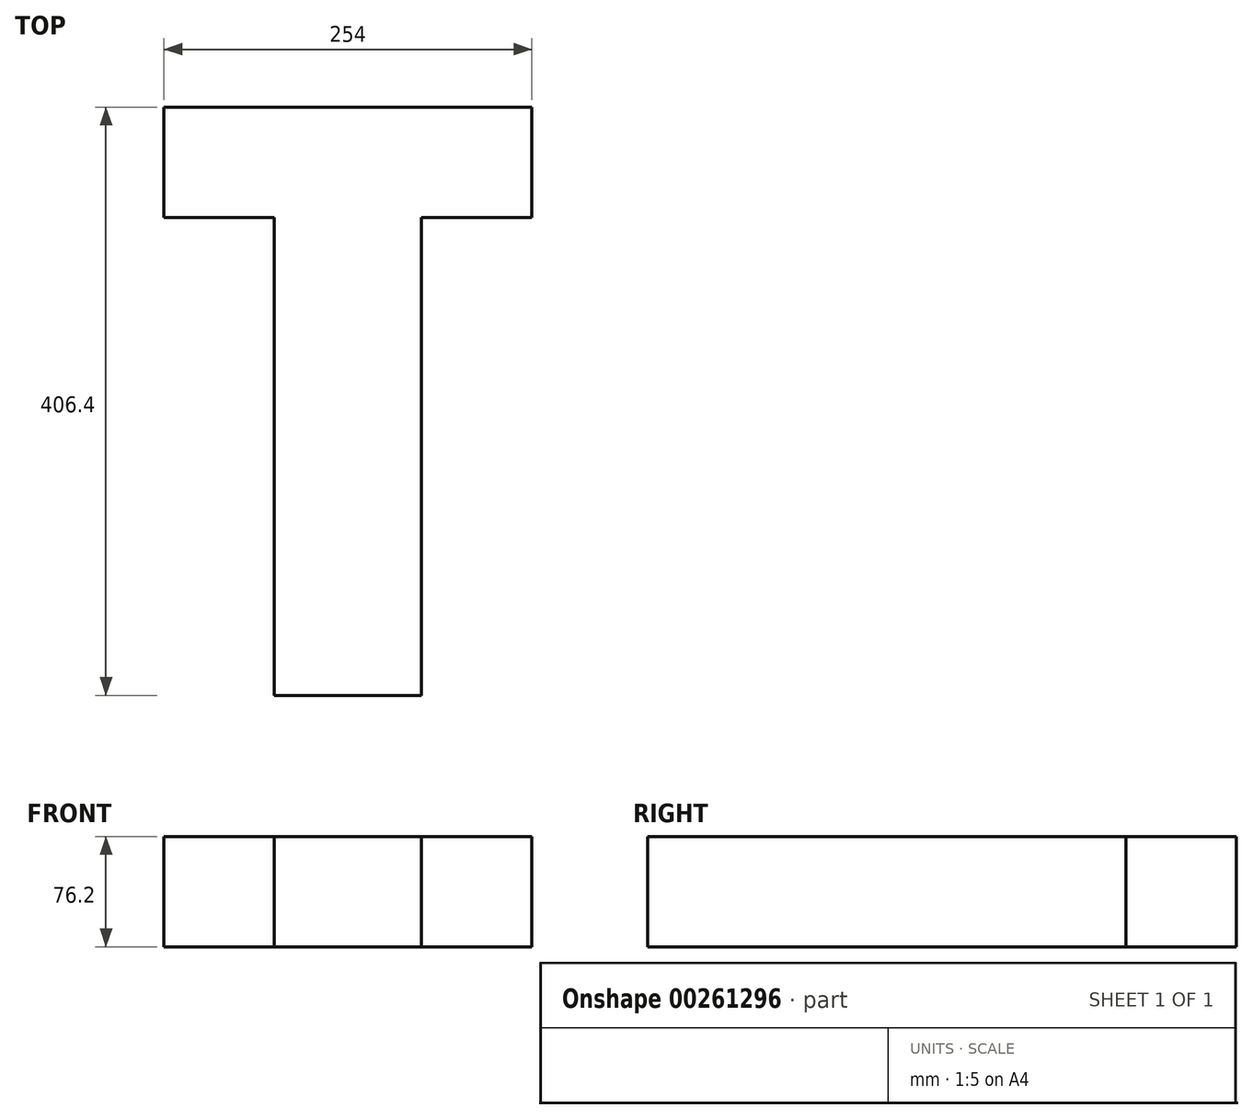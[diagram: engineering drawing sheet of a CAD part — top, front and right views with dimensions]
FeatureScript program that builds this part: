
annotation { "Feature Type Name" : "Feature", "Feature Type Description" : "" }
export const myFeature = defineFeature(function(context is Context, id is Id, definition is map)
    precondition{}
    {
        {
            var Q0;
            Q0=qCreatedBy(makeId("Top.planeOp"),FACE);
            var sketch = newSketch(context, id + "F0", { "sketchPlane" : qUnion([Q0])});
            skLineSegment(sketch, "E0", {"start": v(-127, 155.68) * mm, "end": v(127, 155.68) * mm});
            skLineSegment(sketch, "E1", {"start": v(127, 155.68) * mm, "end": v(127, 79.48) * mm});
            skLineSegment(sketch, "E2", {"start": v(127, 79.48) * mm, "end": v(50.8, 79.48) * mm});
            skLineSegment(sketch, "E3", {"start": v(50.8, 79.48) * mm, "end": v(50.8, -250.72) * mm});
            skLineSegment(sketch, "E4", {"start": v(50.8, -250.72) * mm, "end": v(-50.8, -250.72) * mm});
            skLineSegment(sketch, "E5", {"start": v(-50.8, -250.72) * mm, "end": v(-50.8, 79.48) * mm});
            skLineSegment(sketch, "E6", {"start": v(-50.8, 79.48) * mm, "end": v(-127, 79.48) * mm});
            skLineSegment(sketch, "E7", {"start": v(-127, 79.48) * mm, "end": v(-127, 155.68) * mm});
            skSolve(sketch);
        }
        {
            var Q0;
            Q0=makeQuery(id+"F0.imprint","IMPRINT",FACE,{"disambiguationData":[TD([[makeQuery(id+"F0.imprint","IMPRINT",EDGE,{"derivedFrom":sQuery(id+"F0.wireOp",EDGE,"E0")}),-1.0]])]});
            extrude(context, id + "F1", {"entities" : qUnion([Q0]), "depth" : 76.2 * mm});
        }
    });
